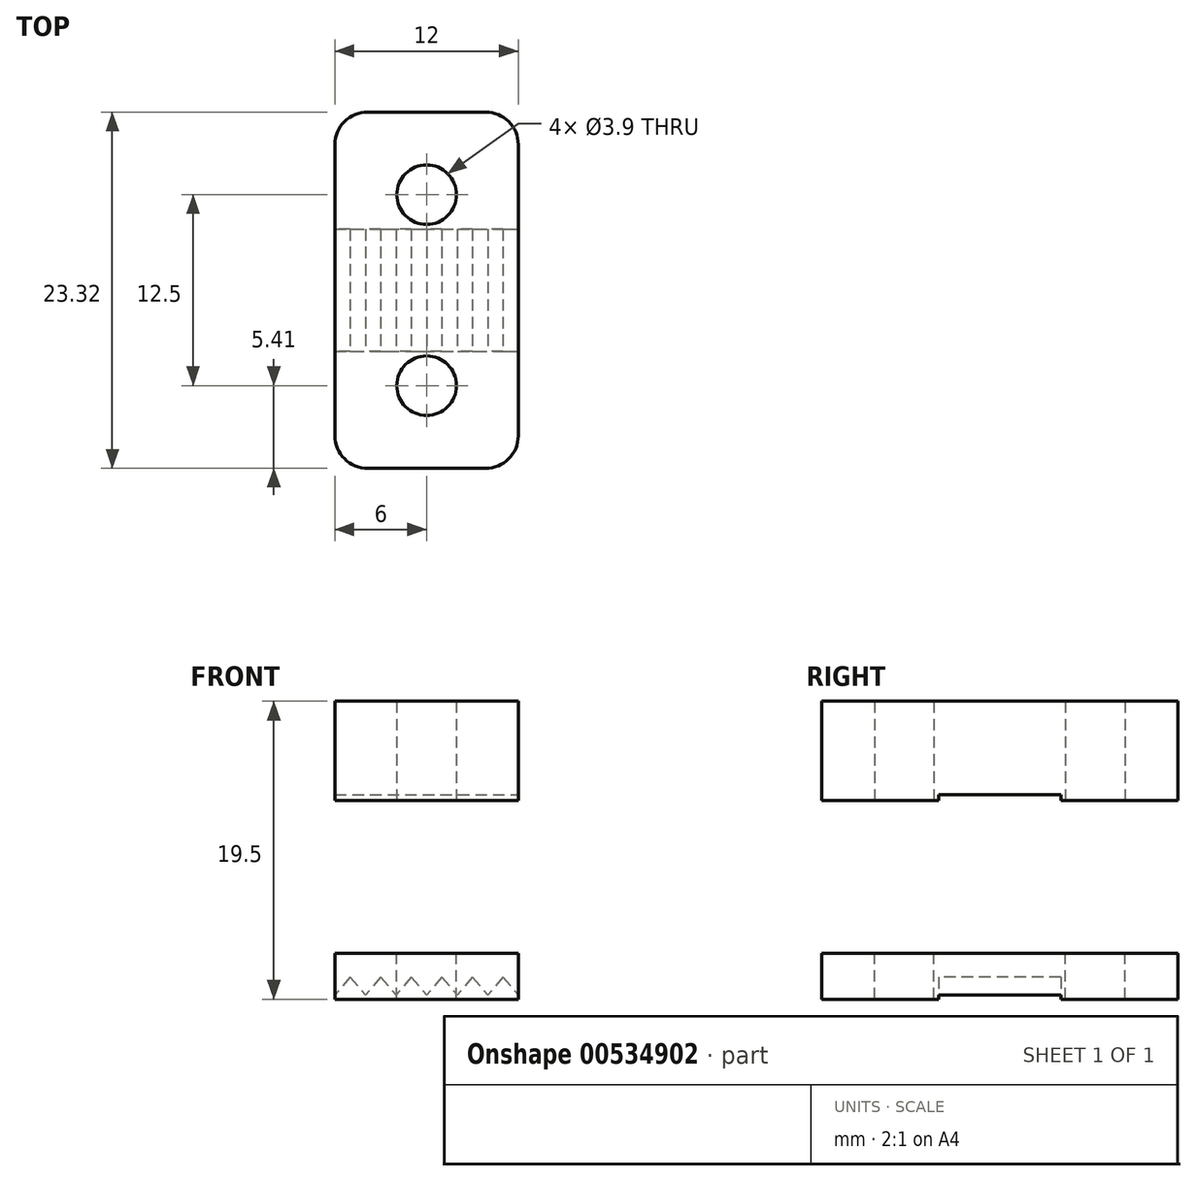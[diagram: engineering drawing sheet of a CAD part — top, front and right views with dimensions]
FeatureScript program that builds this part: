
annotation { "Feature Type Name" : "Feature", "Feature Type Description" : "" }
export const myFeature = defineFeature(function(context is Context, id is Id, definition is map)
    precondition{}
    {
        {
            var Q0;
            Q0=qCreatedBy(makeId("Top.planeOp"),FACE);
            var sketch = newSketch(context, id + "F0", { "sketchPlane" : qUnion([Q0])});
            skCircle(sketch, "E0", {"center": v(0, 6.25) * mm, "radius": 1.95 * mm});
            skLineSegment(sketch, "E1.bottom", {"start": v(-3.85, 11.66) * mm, "end": v(3.85, 11.66) * mm});
            skLineSegment(sketch, "E1.top", {"start": v(-6, 0) * mm, "end": v(6, 0) * mm});
            skLineSegment(sketch, "E1.left", {"start": v(-6, 9.52) * mm, "end": v(-6, 0) * mm});
            skLineSegment(sketch, "E1.right", {"start": v(6, 9.52) * mm, "end": v(6, 0) * mm});
            skPoint(sketch, "E2.visualSharp", {"position": v(-6, 11.66) * mm});
            skArc(sketch, "E2.filletArc", {"start": v(-3.85, 11.66) * mm, "mid": v(-5.37, 11.03) * mm, "end": v(-6, 9.52) * mm});
            skPoint(sketch, "E3.visualSharp", {"position": v(6, 11.66) * mm});
            skArc(sketch, "E3.filletArc", {"start": v(6, 9.52) * mm, "mid": v(5.37, 11.03) * mm, "end": v(3.85, 11.66) * mm});
            skSolve(sketch);
        }
        {
            var Q0;
            Q0=makeQuery(id+"F0.imprint","IMPRINT",FACE,{"disambiguationData":[TD([[makeQuery(id+"F0.imprint","IMPRINT",EDGE,{"derivedFrom":sQuery(id+"F0.wireOp",EDGE,"E0")}),-1.0]])]});
            extrude(context, id + "F1", {"entities" : qUnion([Q0]), "depth" : 6.5 * mm});
        }
        {
            var Q0;
            Q0=makeQuery(id+"F1.opExtrude","SWEPT_BODY",BODY,{"disambiguationData":[OSD([sQuery(id+"F0.wireOp",EDGE,"E0"),sQuery(id+"F0.wireOp",EDGE,"E1.bottom"),sQuery(id+"F0.wireOp",EDGE,"E1.top"),sQuery(id+"F0.wireOp",EDGE,"E1.left"),sQuery(id+"F0.wireOp",EDGE,"E1.right"),sQuery(id+"F0.wireOp",EDGE,"E2.filletArc"),sQuery(id+"F0.wireOp",EDGE,"E3.filletArc")])]});
            var Q1;
            Q1=qCreatedBy(makeId("Front.planeOp"),FACE);
            mirror(context, id + "F2", {"operationType" : NewBodyOperationType.ADD, "entities" : qUnion([Q0]), "mirrorPlane" : qUnion([Q1])});
        }
        {
            var Q0;
            Q0=qCreatedBy(makeId("Top.planeOp"),FACE);
            cPlane(context, id + "F3", {"entities" : qUnion([Q0]), "cplaneType" : CPlaneType.OFFSET, "offset" : 10 * mm, "oppositeDirection" : true, "width" : 150 * mm, "height" : 150 * mm});
        }
        {
            var Q0;
            Q0=qCreatedBy(id+"F3.planeOp",FACE);
            var sketch = newSketch(context, id + "F4", { "sketchPlane" : qUnion([Q0])});
            skCircle(sketch, "E4.0", {"center": v(0, -6.25) * mm, "radius": 1.95 * mm});
            skCircle(sketch, "E5.0", {"center": v(0, 6.25) * mm, "radius": 1.95 * mm});
            skLineSegment(sketch, "E6.0", {"start": v(-6, 9.52) * mm, "end": v(-6, -9.52) * mm});
            skArc(sketch, "E7.0", {"start": v(-3.85, -11.66) * mm, "mid": v(-5.37, -11.03) * mm, "end": v(-6, -9.52) * mm});
            skLineSegment(sketch, "E8.0", {"start": v(-3.85, -11.66) * mm, "end": v(3.85, -11.66) * mm});
            skPoint(sketch, "E9.0", {"position": v(5.37, -11.03) * mm});
            skArc(sketch, "E10.0", {"start": v(6, -9.52) * mm, "mid": v(5.37, -11.03) * mm, "end": v(3.85, -11.66) * mm});
            skLineSegment(sketch, "E11.0", {"start": v(6, 9.52) * mm, "end": v(6, -9.52) * mm});
            skArc(sketch, "E12.0", {"start": v(6, 9.52) * mm, "mid": v(5.37, 11.03) * mm, "end": v(3.85, 11.66) * mm});
            skLineSegment(sketch, "E13.0", {"start": v(-3.85, 11.66) * mm, "end": v(3.85, 11.66) * mm});
            skArc(sketch, "E14.0", {"start": v(-3.85, 11.66) * mm, "mid": v(-5.37, 11.03) * mm, "end": v(-6, 9.52) * mm});
            skSolve(sketch);
        }
        {
            var Q0;
            Q0=makeQuery(id+"F4.imprint","IMPRINT",FACE,{"disambiguationData":[TD([[makeQuery(id+"F4.imprint","IMPRINT",EDGE,{"derivedFrom":sQuery(id+"F4.wireOp",EDGE,"E4.0")}),-1.0]])]});
            extrude(context, id + "F5", {"entities" : qUnion([Q0]), "oppositeDirection" : true, "depth" : 3 * mm});
        }
        {
            var Q0;
            Q0=qCreatedBy(makeId("Front.planeOp"),FACE);
            var sketch = newSketch(context, id + "F6", { "sketchPlane" : qUnion([Q0])});
            skLineSegment(sketch, "E15.0", {"start": v(-6, -13) * mm, "end": v(-6, -12.73) * mm});
            skLineSegment(sketch, "E16.bottom", {"start": v(-6, -13) * mm, "end": v(-4, -13) * mm});
            skLineSegment(sketch, "E16.right", {"start": v(-4, -13) * mm, "end": v(-4, -12.73) * mm});
            skPoint(sketch, "E17", {"position": v(-5, -11.55) * mm});
            skLineSegment(sketch, "E18", {"start": v(-5, -11.55) * mm, "end": v(-4, -12.73) * mm});
            skLineSegment(sketch, "E19", {"start": v(-5, -11.55) * mm, "end": v(-6, -12.73) * mm});
            skPoint(sketch, "E20.orphan", {"position": v(-4, -11.55) * mm});
            skLineSegment(sketch, "E21.trimOffspring", {"start": v(-6, -11.55) * mm, "end": v(-6, -10) * mm});
            skLineSegment(sketch, "E22.1.0.0", {"start": v(-3, -11.55) * mm, "end": v(-2, -12.73) * mm});
            skLineSegment(sketch, "E22.1.0.1", {"start": v(-3, -11.55) * mm, "end": v(-4, -12.73) * mm});
            skLineSegment(sketch, "E22.1.0.3", {"start": v(-4, -13) * mm, "end": v(-2, -13) * mm});
            skLineSegment(sketch, "E22.1.0.4", {"start": v(-2, -13) * mm, "end": v(-2, -12.73) * mm});
            skLineSegment(sketch, "E22.2.0.0", {"start": v(-1, -11.55) * mm, "end": v(0, -12.73) * mm});
            skLineSegment(sketch, "E22.2.0.1", {"start": v(-1, -11.55) * mm, "end": v(-2, -12.73) * mm});
            skLineSegment(sketch, "E22.2.0.2", {"start": v(-2, -13) * mm, "end": v(-2, -12.73) * mm});
            skLineSegment(sketch, "E22.2.0.3", {"start": v(-2, -13) * mm, "end": v(0, -13) * mm});
            skLineSegment(sketch, "E22.2.0.4", {"start": v(0, -13) * mm, "end": v(0, -12.73) * mm});
            skLineSegment(sketch, "E22.3.0.0", {"start": v(1, -11.55) * mm, "end": v(2, -12.73) * mm});
            skLineSegment(sketch, "E22.3.0.1", {"start": v(1, -11.55) * mm, "end": v(0, -12.73) * mm});
            skLineSegment(sketch, "E22.3.0.2", {"start": v(0, -13) * mm, "end": v(0, -12.73) * mm});
            skLineSegment(sketch, "E22.3.0.3", {"start": v(0, -13) * mm, "end": v(2, -13) * mm});
            skLineSegment(sketch, "E22.3.0.4", {"start": v(2, -13) * mm, "end": v(2, -12.73) * mm});
            skLineSegment(sketch, "E22.4.0.0", {"start": v(3, -11.55) * mm, "end": v(4, -12.73) * mm});
            skLineSegment(sketch, "E22.4.0.1", {"start": v(3, -11.55) * mm, "end": v(2, -12.73) * mm});
            skLineSegment(sketch, "E22.4.0.2", {"start": v(2, -13) * mm, "end": v(2, -12.73) * mm});
            skLineSegment(sketch, "E22.4.0.3", {"start": v(2, -13) * mm, "end": v(4, -13) * mm});
            skLineSegment(sketch, "E22.4.0.4", {"start": v(4, -13) * mm, "end": v(4, -12.73) * mm});
            skLineSegment(sketch, "E22.5.0.0", {"start": v(5, -11.55) * mm, "end": v(6, -12.73) * mm});
            skLineSegment(sketch, "E22.5.0.1", {"start": v(5, -11.55) * mm, "end": v(4, -12.73) * mm});
            skLineSegment(sketch, "E22.5.0.2", {"start": v(4, -13) * mm, "end": v(4, -12.73) * mm});
            skLineSegment(sketch, "E22.5.0.3", {"start": v(4, -13) * mm, "end": v(6, -13) * mm});
            skLineSegment(sketch, "E22.5.0.4", {"start": v(6, -13) * mm, "end": v(6, -12.73) * mm});
            skLineSegment(sketch, "E22.direction1", {"start": v(-4, -12.73) * mm, "end": v(-2, -12.73) * mm, "construction": true});
            skSolve(sketch);
        }
        {
            var Q0;
            Q0=qSketchRegion(id+"F6",true);
            extrude(context, id + "F7", {"entities" : qUnion([Q0]), "operationType" : NewBodyOperationType.REMOVE, "oppositeDirection" : true, "depth" : 4 * mm, "hasSecondDirection" : true, "secondDirectionOppositeDirection" : false, "secondDirectionDepth" : 4 * mm});
        }
        {
            var Q0;
            Q0=qCreatedBy(makeId("Top.planeOp"),FACE);
            var sketch = newSketch(context, id + "F8", { "sketchPlane" : qUnion([Q0])});
            skLineSegment(sketch, "E23.0", {"start": v(-6, 9.52) * mm, "end": v(-6, -9.52) * mm});
            skLineSegment(sketch, "E24.0", {"start": v(6, 9.52) * mm, "end": v(6, -9.52) * mm});
            skLineSegment(sketch, "E25.bottom", {"start": v(-6, 4) * mm, "end": v(6, 4) * mm});
            skLineSegment(sketch, "E25.top", {"start": v(-6, 0) * mm, "end": v(6, 0) * mm});
            skLineSegment(sketch, "E25.left", {"start": v(-6, 4) * mm, "end": v(-6, 0) * mm});
            skLineSegment(sketch, "E25.right", {"start": v(6, 4) * mm, "end": v(6, 0) * mm});
            skLineSegment(sketch, "E26.MirrorCS", {"start": v(-6, -4) * mm, "end": v(6, -4) * mm});
            skSolve(sketch);
        }
        {
            var Q0;
            Q0=makeQuery(id+"F8.imprint","IMPRINT",FACE,{"disambiguationData":[TD([[makeQuery(id+"F8.imprint","IMPRINT",EDGE,{"derivedFrom":sQuery(id+"F8.wireOp",EDGE,"E25.bottom")}),-1.0]])]});
            var Q1;
            {var subQ0=sQuery(id+"F8.wireOp",EDGE,"E25.top");Q1=makeQuery(id+"F8.imprint","IMPRINT",FACE,{"disambiguationData":[TD([[makeQuery(id+"F8.imprint","IMPRINT",EDGE,{"derivedFrom":subQ0}),-1.0]])]});}
            extrude(context, id + "F9", {"entities" : qUnion([Q0, Q1]), "operationType" : NewBodyOperationType.REMOVE, "depth" : 0.4 * mm});
        }
    });
